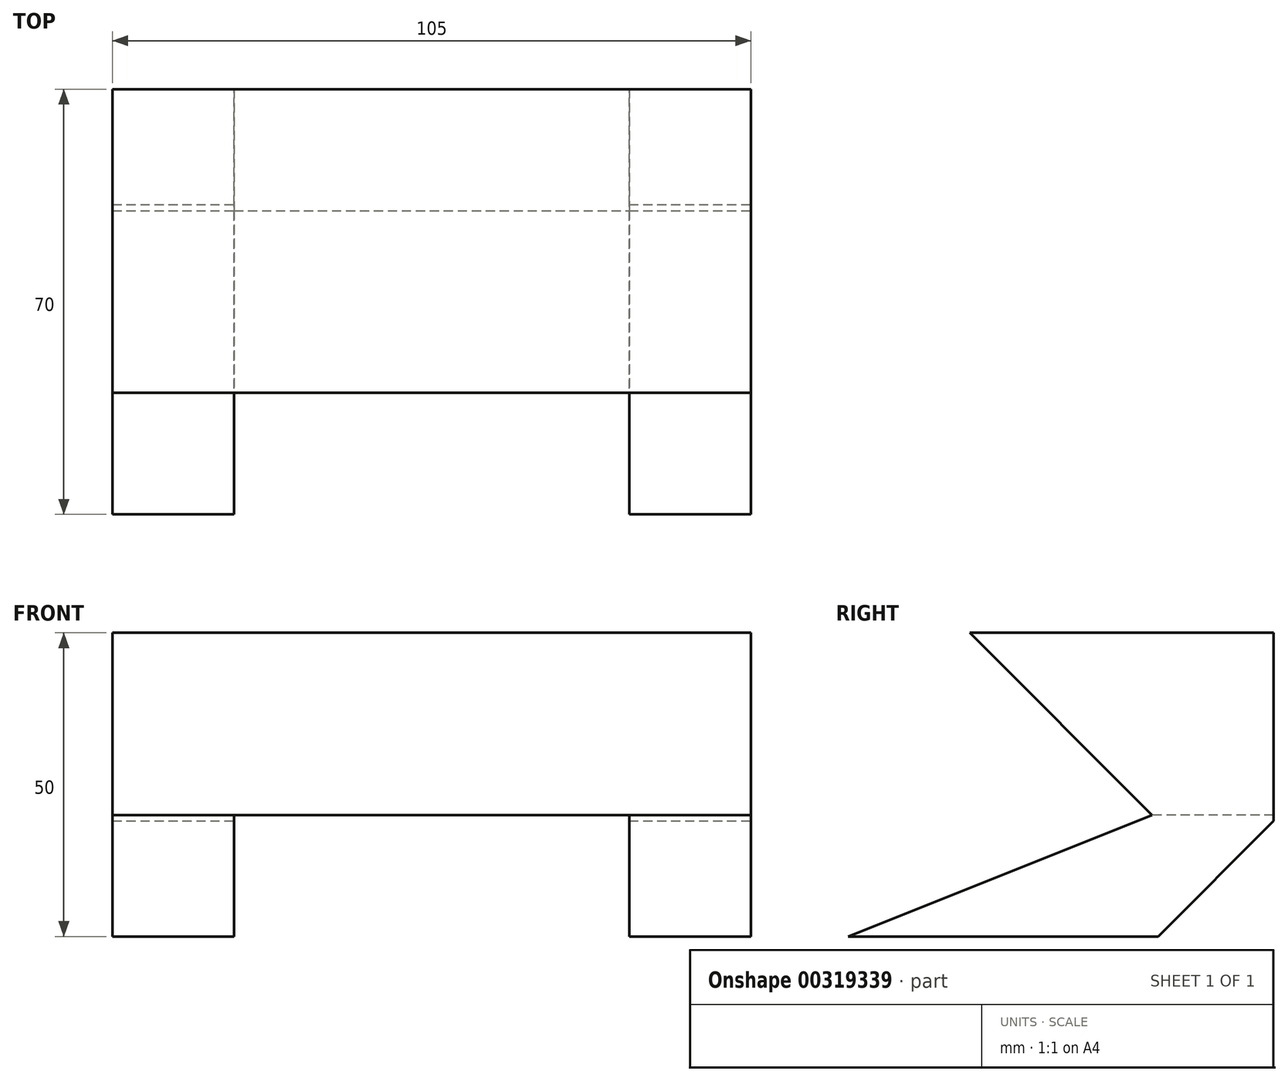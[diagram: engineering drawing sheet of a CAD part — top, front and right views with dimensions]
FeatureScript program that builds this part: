
annotation { "Feature Type Name" : "Feature", "Feature Type Description" : "" }
export const myFeature = defineFeature(function(context is Context, id is Id, definition is map)
    precondition{}
    {
        {
            var Q0;
            Q0=qCreatedBy(makeId("Top.planeOp"),FACE);
            var sketch = newSketch(context, id + "F0", { "sketchPlane" : qUnion([Q0])});
            skLineSegment(sketch, "E0.bottom", {"start": v(52.5, -35) * mm, "end": v(-52.5, -35) * mm});
            skLineSegment(sketch, "E0.top", {"start": v(52.5, 35) * mm, "end": v(-52.5, 35) * mm});
            skLineSegment(sketch, "E0.left", {"start": v(52.5, -35) * mm, "end": v(52.5, 35) * mm});
            skLineSegment(sketch, "E0.right", {"start": v(-52.5, -35) * mm, "end": v(-52.5, 35) * mm});
            skPoint(sketch, "E0.middle", {"position": v(0, 0) * mm});
            skSolve(sketch);
        }
        {
            var Q0;
            Q0 = qSketchRegion(id + "F0", true);
            extrude(context, id + "F1", {"entities" : qUnion([Q0]), "depth" : 50 * mm});
        }
        {
            var Q0;
            Q0=makeQuery(id+"F1.opExtrude","SWEPT_FACE",FACE,{"disambiguationData":[OSD([sQuery(id+"F0.wireOp",EDGE,"E0.left")])]});
            var sketch = newSketch(context, id + "F2", { "sketchPlane" : qUnion([Q0])});
            skLineSegment(sketch, "E1", {"start": v(35, 0) * mm, "end": v(16, 0) * mm});
            skPoint(sketch, "E1.endSnap0", {"position": v(0, 0) * mm});
            skLineSegment(sketch, "E2", {"start": v(35, 19) * mm, "end": v(35, 0) * mm});
            skLineSegment(sketch, "E3", {"start": v(35, 19) * mm, "end": v(16, 0) * mm});
            skSolve(sketch);
        }
        {
            var Q0;
            Q0 = qSketchRegion(id + "F2", true);
            extrude(context, id + "F3", {"entities" : qUnion([Q0]), "operationType" : NewBodyOperationType.REMOVE, "endBound" : BoundingType.THROUGH_ALL, "oppositeDirection" : true, "depth" : 25 * mm});
        }
        {
            var Q0;
            Q0=makeQuery(id+"F1.opExtrude","SWEPT_FACE",FACE,{"disambiguationData":[OSD([sQuery(id+"F0.wireOp",EDGE,"E0.left")])]});
            var sketch = newSketch(context, id + "F4", { "sketchPlane" : qUnion([Q0])});
            skLineSegment(sketch, "E4", {"start": v(-35, 20) * mm, "end": v(15, 20) * mm});
            skLineSegment(sketch, "E5", {"start": v(15, 20) * mm, "end": v(-44.93, 79.93) * mm});
            skLineSegment(sketch, "E6", {"start": v(-44.93, 79.93) * mm, "end": v(-35, 20) * mm});
            skSolve(sketch);
        }
        {
            var Q0;
            Q0 = qSketchRegion(id + "F4", true);
            extrude(context, id + "F5", {"entities" : qUnion([Q0]), "operationType" : NewBodyOperationType.REMOVE, "endBound" : BoundingType.THROUGH_ALL, "oppositeDirection" : true, "depth" : 25 * mm});
        }
        {
            var Q0;
            Q0=makeQuery(id+"F1.opExtrude","SWEPT_FACE",FACE,{"disambiguationData":[OSD([sQuery(id+"F0.wireOp",EDGE,"E0.bottom")])]});
            var sketch = newSketch(context, id + "F6", { "sketchPlane" : qUnion([Q0])});
            skLineSegment(sketch, "E7.bottom", {"start": v(32.5, -20) * mm, "end": v(-32.5, -20) * mm});
            skLineSegment(sketch, "E7.top", {"start": v(32.5, 20) * mm, "end": v(-32.5, 20) * mm});
            skLineSegment(sketch, "E7.left", {"start": v(32.5, -20) * mm, "end": v(32.5, 20) * mm});
            skLineSegment(sketch, "E7.right", {"start": v(-32.5, -20) * mm, "end": v(-32.5, 20) * mm});
            skPoint(sketch, "E7.middle", {"position": v(0, 0) * mm});
            skSolve(sketch);
        }
        {
            var Q0;
            Q0 = qSketchRegion(id + "F6", true);
            extrude(context, id + "F7", {"entities" : qUnion([Q0]), "operationType" : NewBodyOperationType.REMOVE, "endBound" : BoundingType.THROUGH_ALL, "oppositeDirection" : true, "depth" : 25 * mm});
        }
        {
            var Q0;
            Q0=makeQuery(id+"F1.opExtrude","SWEPT_FACE",FACE,{"disambiguationData":[OSD([sQuery(id+"F0.wireOp",EDGE,"E0.right")])]});
            var sketch = newSketch(context, id + "F8", { "sketchPlane" : qUnion([Q0])});
            skLineSegment(sketch, "E8", {"start": v(35, 20) * mm, "end": v(35, 0) * mm});
            skLineSegment(sketch, "E9", {"start": v(35, 0) * mm, "end": v(-15, 20) * mm});
            skLineSegment(sketch, "E10", {"start": v(-15, 20) * mm, "end": v(35, 20) * mm});
            skSolve(sketch);
        }
        {
            var Q0;
            Q0 = qSketchRegion(id + "F8", true);
            extrude(context, id + "F9", {"entities" : qUnion([Q0]), "operationType" : NewBodyOperationType.REMOVE, "endBound" : BoundingType.THROUGH_ALL, "oppositeDirection" : true, "depth" : 25 * mm});
        }
    });
